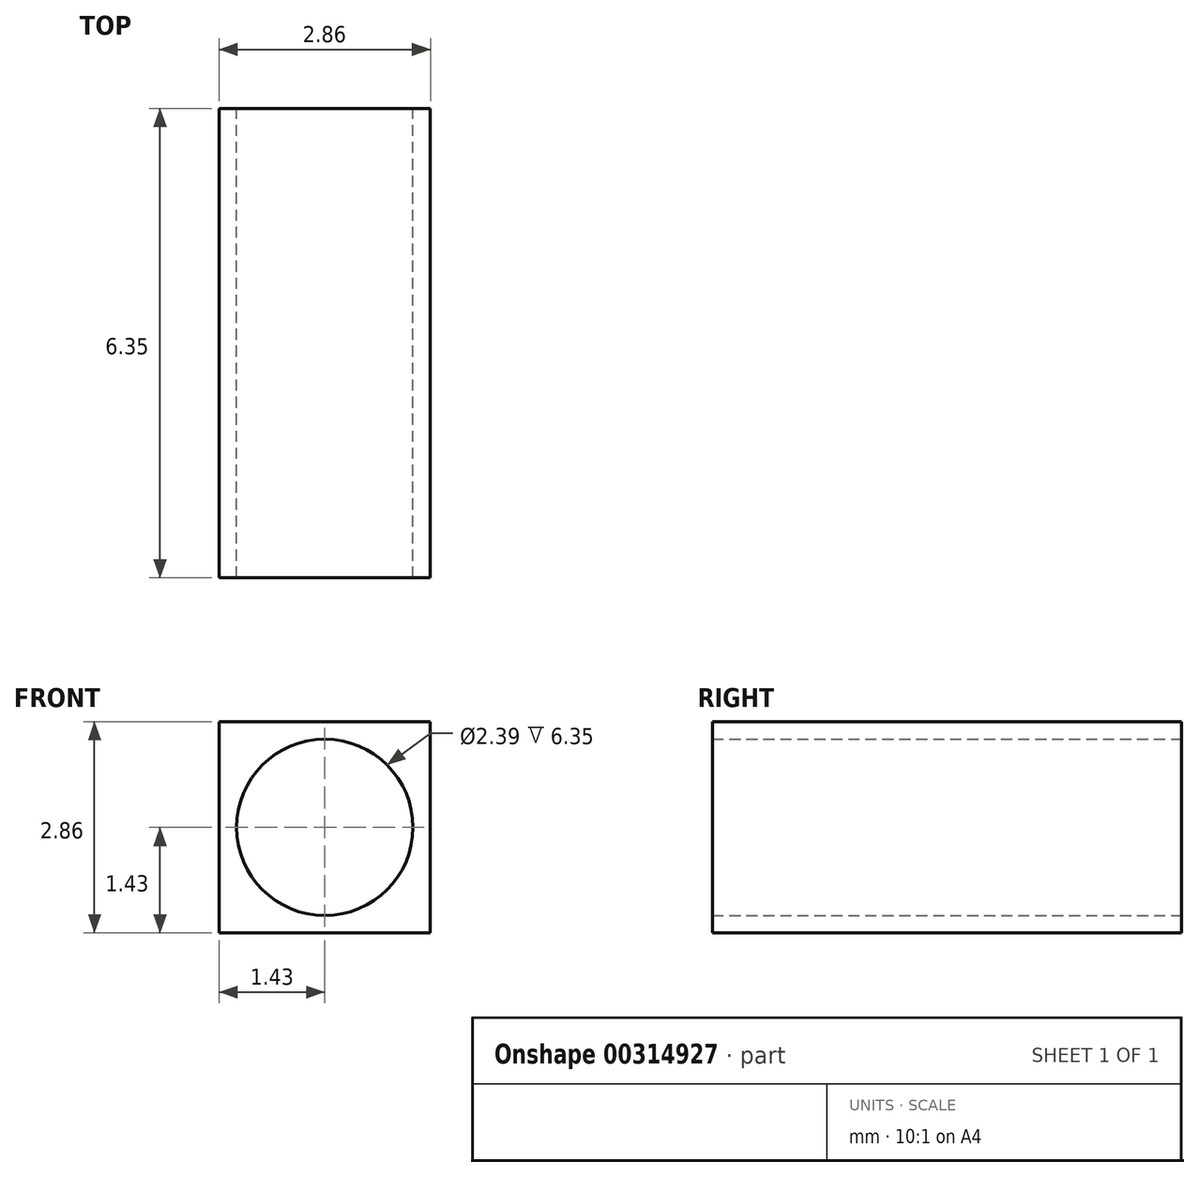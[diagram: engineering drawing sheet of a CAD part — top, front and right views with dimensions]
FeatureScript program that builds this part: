
annotation { "Feature Type Name" : "Feature", "Feature Type Description" : "" }
export const myFeature = defineFeature(function(context is Context, id is Id, definition is map)
    precondition{}
    {
        {
            var Q0;
            Q0=qCreatedBy(makeId("Front.planeOp"),FACE);
            var sketch = newSketch(context, id + "F0", { "sketchPlane" : qUnion([Q0])});
            skLineSegment(sketch, "E0.bottom", {"start": v(1.43, 1.43) * mm, "end": v(-1.43, 1.43) * mm});
            skLineSegment(sketch, "E0.top", {"start": v(1.43, -1.43) * mm, "end": v(-1.43, -1.43) * mm});
            skLineSegment(sketch, "E0.left", {"start": v(1.43, 1.43) * mm, "end": v(1.43, -1.43) * mm});
            skLineSegment(sketch, "E0.right", {"start": v(-1.43, 1.43) * mm, "end": v(-1.43, -1.43) * mm});
            skPoint(sketch, "E0.middle", {"position": v(0, 0) * mm});
            skCircle(sketch, "E1", {"center": v(0, 0) * mm, "radius": 1.2 * mm});
            skSolve(sketch);
        }
        {
            var Q0;
            Q0=makeQuery(id+"F0.imprint","IMPRINT",FACE,{"disambiguationData":[TD([[makeQuery(id+"F0.imprint","IMPRINT",EDGE,{"derivedFrom":sQuery(id+"F0.wireOp",EDGE,"E0.bottom")}),1.0]])]});
            extrude(context, id + "F1", {"entities" : qUnion([Q0]), "depth" : 6.35 * mm});
        }
    });
